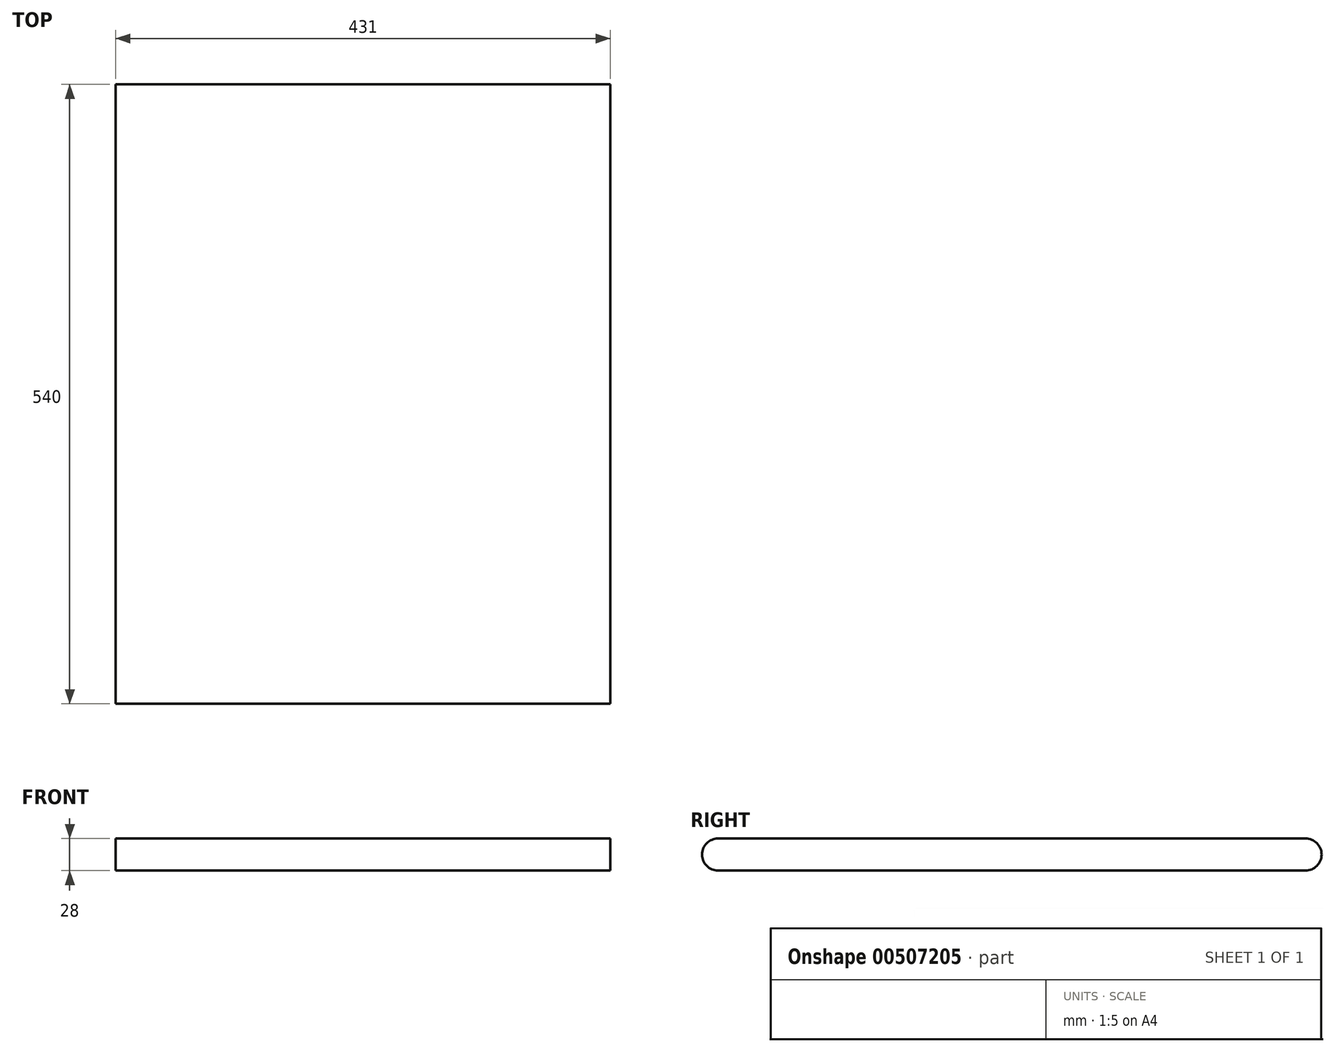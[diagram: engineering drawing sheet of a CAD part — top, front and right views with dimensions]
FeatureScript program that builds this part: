
annotation { "Feature Type Name" : "Feature", "Feature Type Description" : "" }
export const myFeature = defineFeature(function(context is Context, id is Id, definition is map)
    precondition{}
    {
        {
            var Q0;
            Q0=qCreatedBy(makeId("Right.planeOp"),FACE);
            var sketch = newSketch(context, id + "F0", { "sketchPlane" : qUnion([Q0])});
            skLineSegment(sketch, "E0.bottom", {"start": v(-67.53, 8.5) * mm, "end": v(472.47, 8.5) * mm});
            skLineSegment(sketch, "E0.top", {"start": v(-67.53, -19.5) * mm, "end": v(472.47, -19.5) * mm});
            skLineSegment(sketch, "E0.left", {"start": v(-67.53, 8.5) * mm, "end": v(-67.53, -19.5) * mm});
            skLineSegment(sketch, "E0.right", {"start": v(472.47, 8.5) * mm, "end": v(472.47, -19.5) * mm});
            skSolve(sketch);
        }
        {
            var Q0;
            Q0 = qSketchRegion(id + "F0", true);
            extrude(context, id + "F1", {"entities" : qUnion([Q0]), "depth" : 431 * mm});
        }
        {
            var Q0;
            Q0=makeQuery(id+"F1.opExtrude","SWEPT_EDGE",EDGE,{"disambiguationData":[OSD([sQuery(id+"F0.wireOp",EDGE,"E0.bottom"),sQuery(id+"F0.wireOp",EDGE,"E0.left")])]});
            var Q1;
            Q1=makeQuery(id+"F1.opExtrude","SWEPT_EDGE",EDGE,{"disambiguationData":[OSD([sQuery(id+"F0.wireOp",EDGE,"E0.top"),sQuery(id+"F0.wireOp",EDGE,"E0.left")])]});
            var Q2;
            Q2=makeQuery(id+"F1.opExtrude","SWEPT_EDGE",EDGE,{"disambiguationData":[OSD([sQuery(id+"F0.wireOp",EDGE,"E0.bottom"),sQuery(id+"F0.wireOp",EDGE,"E0.right")])]});
            var Q3;
            Q3=makeQuery(id+"F1.opExtrude","SWEPT_EDGE",EDGE,{"disambiguationData":[OSD([sQuery(id+"F0.wireOp",EDGE,"E0.top"),sQuery(id+"F0.wireOp",EDGE,"E0.right")])]});
            fillet(context, id + "F2", {"entities" : qUnion([Q0, Q1, Q2, Q3]), "radius" : 14 * mm, "tangentPropagation" : true, "allowEdgeOverflow" : false});
        }
    });
